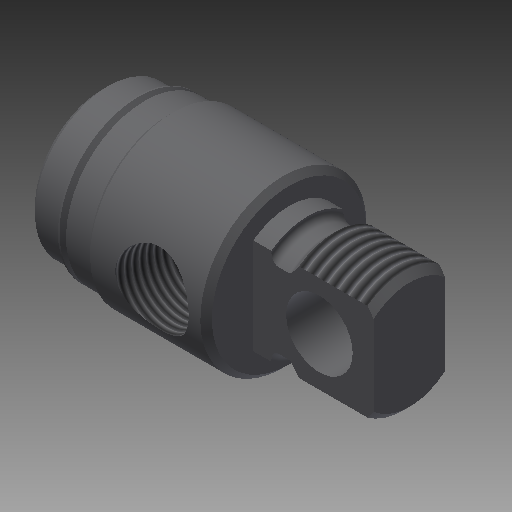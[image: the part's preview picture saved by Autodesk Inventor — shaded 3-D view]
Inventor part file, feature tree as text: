
AUTODESK INVENTOR PART (.ipt)
format: ipt  version: 2018 (Build 220112000, 112)  size: 340,992 bytes
history: native  units: in
note: dims shown in document units (in); Inventor stores cm internally (conversion verified against a paired STEP export)
features: other x154, sketch x7, revolve x5, thread x2, extrude x2
ambient origin geometry x8: Origin, YZ Plane, XZ Plane, XY Plane, X Axis, Y Axis, Z Axis, Center Point
bodies: Solid1 (feature_tree)
feature tree (170):
  revolve  "Revolution1"  Angle=360.0deg
  revolve  "Revolution2"  [1 undecoded]
  thread  "Thread1"  [1 undecoded]
  extrude  "Extrusion1"  Depth=0.3021in TaperAngle=0.0deg
  revolve  "Revolution3"  [1 undecoded]
  revolve  "Revolution4"  [1 undecoded]
  thread  "Thread2"  [1 undecoded]
  revolve  "Revolution5"  [1 undecoded]
  extrude  "Extrusion2"  [1 undecoded]
  other  "1_XY"
  other  "1_YZ"
  other  "1_ZX"
  other  "1_X"
  other  "1_Y"
  other  "1_Z"
  other  "1_Center"
  other  "c1_XY"
  other  "c1_YZ"
  other  "c1_ZX"
  other  "c1_X"
  other  "c1_Y"
  other  "c1_Z"
  other  "c1_Center"
  other  "c2_XY"
  other  "c2_YZ"
  other  "c2_ZX"
  other  "c2_X"
  other  "c2_Y"
  other  "c2_Z"
  other  "c2_Center"
  other  "cc1_XY"
  other  "cc1_YZ"
  other  "cc1_ZX"
  other  "cc1_X"
  other  "cc1_Y"
  other  "cc1_Z"
  other  "cc1_Center"
  other  "cc2_XY"
  other  "cc2_YZ"
  other  "cc2_ZX"
  other  "cc2_X"
  other  "cc2_Y"
  other  "cc2_Z"
  other  "cc2_Center"
  other  "lovra1_XY"
  other  "lovra1_YZ"
  other  "lovra1_ZX"
  other  "lovra1_X"
  other  "lovra1_Y"
  other  "lovra1_Z"
  other  "lovra1_Center"
  other  "lovra2_XY"
  other  "lovra2_YZ"
  other  "lovra2_ZX"
  other  "lovra2_X"
  other  "lovra2_Y"
  other  "lovra2_Z"
  other  "lovra2_Center"
  other  "lovra21_XY"
  other  "lovra21_YZ"
  other  "lovra21_ZX"
  other  "lovra21_X"
  other  "lovra21_Y"
  other  "lovra21_Z"
  other  "lovra21_Center"
  other  "lovra22_XY"
  other  "lovra22_YZ"
  other  "lovra22_ZX"
  other  "lovra22_X"
  other  "lovra22_Y"
  other  "lovra22_Z"
  other  "lovra22_Center"
  other  "lovra3_XY"
  other  "lovra3_YZ"
  other  "lovra3_ZX"
  other  "lovra3_X"
  other  "lovra3_Y"
  other  "lovra3_Z"
  other  "lovra3_Center"
  other  "olen_XY"
  other  "olen_YZ"
  other  "olen_ZX"
  other  "olen_X"
  other  "olen_Y"
  other  "olen_Z"
  other  "olen_Center"
  other  "p1_XY"
  other  "p1_YZ"
  other  "p1_ZX"
  other  "p1_X"
  other  "p1_Y"
  other  "p1_Z"
  other  "p1_Center"
  other  "p2_XY"
  other  "p2_YZ"
  other  "p2_ZX"
  other  "p2_X"
  other  "p2_Y"
  other  "p2_Z"
  other  "p2_Center"
  other  "port_XY"
  other  "port_YZ"
  other  "port_ZX"
  other  "port_X"
  other  "port_Y"
  other  "port_Z"
  other  "port_Center"
  other  "port2_XY"
  other  "port2_YZ"
  other  "port2_ZX"
  other  "port2_X"
  other  "port2_Y"
  other  "port2_Z"
  other  "port2_Center"
  other  "thd1_XY"
  other  "thd1_YZ"
  other  "thd1_ZX"
  other  "thd1_X"
  other  "thd1_Y"
  other  "thd1_Z"
  other  "thd1_Center"
  other  "thd2_XY"
  other  "thd2_YZ"
  other  "thd2_ZX"
  other  "thd2_X"
  other  "thd2_Y"
  other  "thd2_Z"
  other  "thd2_Center"
  other  "to_mounting_bracket_XY"
  other  "to_mounting_bracket_YZ"
  other  "to_mounting_bracket_ZX"
  other  "to_mounting_bracket_X"
  other  "to_mounting_bracket_Y"
  other  "to_mounting_bracket_Z"
  other  "to_mounting_bracket_Center"
  other  "to_nut_XY"
  other  "to_nut_YZ"
  other  "to_nut_ZX"
  other  "to_nut_X"
  other  "to_nut_Y"
  other  "to_nut_Z"
  other  "to_nut_Center"
  other  "to_pin_XY"
  other  "to_pin_YZ"
  other  "to_pin_ZX"
  other  "to_pin_X"
  other  "to_pin_Y"
  other  "to_pin_Z"
  other  "to_pin_Center"
  other  "to_screw_XY"
  other  "to_screw_YZ"
  other  "to_screw_ZX"
  other  "to_screw_X"
  other  "to_screw_Y"
  other  "to_screw_Z"
  other  "to_screw_Center"
  other  "to_tube_XY"
  other  "to_tube_YZ"
  other  "to_tube_ZX"
  other  "to_tube_X"
  other  "to_tube_Y"
  other  "to_tube_Z"
  other  "to_tube_Center"
  sketch  "Sketch_8"  dims[d7=360.0deg d8=0.3021in d9=0.0in]
  sketch  "Sketch_15"  dims[d13=0.0in d14=0.0in d15=0.0in d16=0.0in]
  sketch  "Sketch_9"  dims[d10=360.0deg d11=0.5587in d12=0.0in]
  sketch  "Sketch_13_ALT_Drilling_1"  dims[d0=360.0deg d1=360.0deg]
  sketch  "Sketch_68_ALT_Drilling_2"  dims[d2=0.3547in d3=0.0in d4=0.625in d5=0.0in d6=360.0deg]
  sketch  "Sketch_24"
  sketch  "Sketch_43"
note: 7 required parameter values undecoded (feature->parameter linkage not recoverable at this tier; creation-order binding heuristic only, values carry confidence <= 0.55)